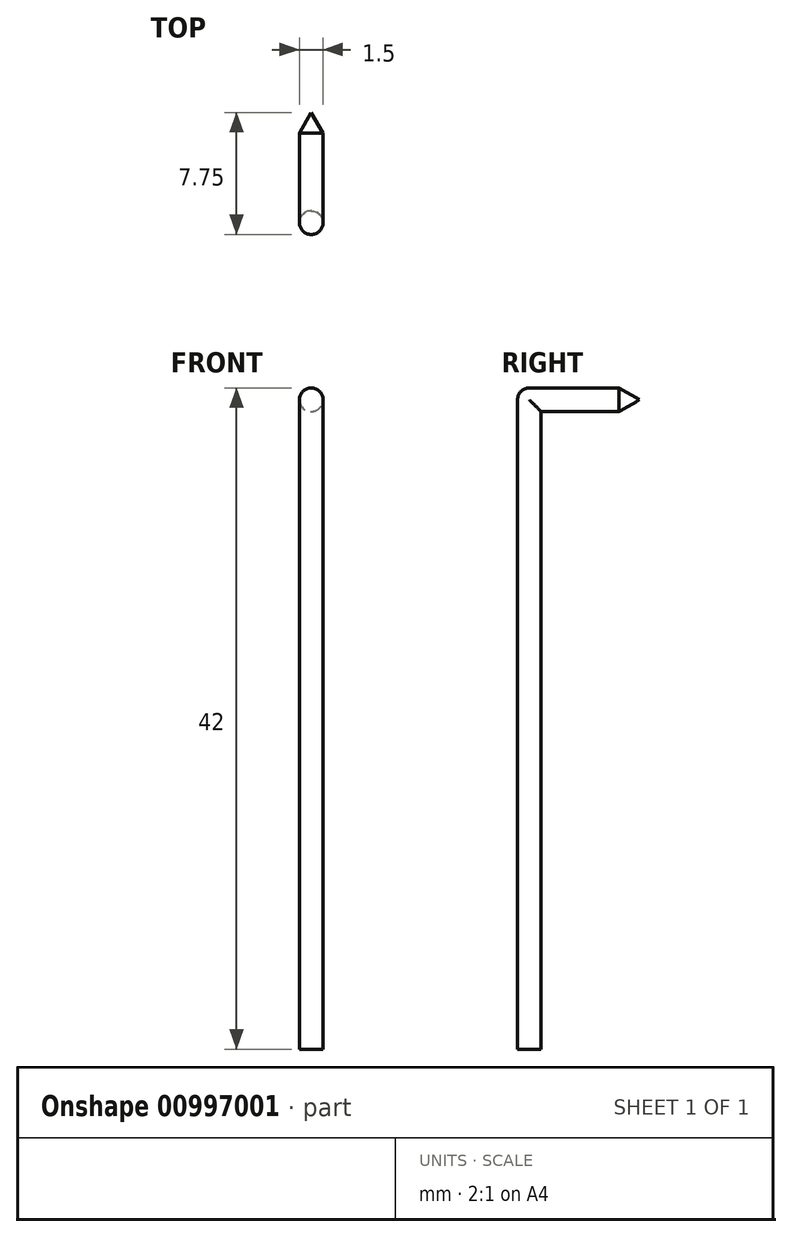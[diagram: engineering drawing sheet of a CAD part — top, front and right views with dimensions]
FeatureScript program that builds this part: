
annotation { "Feature Type Name" : "Feature", "Feature Type Description" : "" }
export const myFeature = defineFeature(function(context is Context, id is Id, definition is map)
    precondition{}
    {
        {
            var Q0;
            Q0=qCreatedBy(makeId("Top.planeOp"),FACE);
            var sketch = newSketch(context, id + "F0", { "sketchPlane" : qUnion([Q0])});
            skCircle(sketch, "E0", {"center": v(0, 0) * mm, "radius": 0.75 * mm});
            skLineSegment(sketch, "E1.bottom", {"start": v(-0.75, 0) * mm, "end": v(0.75, 0) * mm});
            skLineSegment(sketch, "E1.top", {"start": v(-0.75, 7) * mm, "end": v(0.75, 7) * mm});
            skLineSegment(sketch, "E1.left", {"start": v(-0.75, 0) * mm, "end": v(-0.75, 7) * mm});
            skLineSegment(sketch, "E1.right", {"start": v(0.75, 0) * mm, "end": v(0.75, 7) * mm});
            skSolve(sketch);
        }
        {
            var Q0;
            Q0=makeQuery(id+"F0.imprint","IMPRINT",FACE,{"disambiguationData":[TD([[makeQuery(id+"F0.imprint","IMPRINT",EDGE,{"derivedFrom":sQuery(id+"F0.wireOp",EDGE,"E0")}),1.0]])]});
            extrude(context, id + "F1", {"entities" : qUnion([Q0]), "depth" : 42 * mm, "offsetDistance" : 25 * mm});
        }
        {
            var Q0;
            Q0=makeQuery(id+"F0.imprint","IMPRINT",FACE,{"disambiguationData":[TD([[makeQuery(id+"F0.imprint","IMPRINT",EDGE,{"derivedFrom":sQuery(id+"F0.wireOp",EDGE,"E1.top")}),-1.0]])]});
            extrude(context, id + "F2", {"entities" : qUnion([Q0]), "operationType" : NewBodyOperationType.ADD, "depth" : 42 * mm, "offsetDistance" : 25 * mm, "hasSecondDirection" : true, "secondDirectionOppositeDirection" : false, "secondDirectionDepth" : 40.5 * mm});
        }
        {
            var Q0;
            {var subQ0=sQuery(id+"F0.wireOp",EDGE,"E1.top");Q0=makeQuery(id+"F0powoGMsJJjLha_1.opChamfer","BLEND_EDGE",EDGE,{"blendedFrom":[makeQuery(id+"F2.opExtrude","SWEPT_EDGE",EDGE,{"disambiguationData":[OSD([subQ0,sQuery(id+"F0.wireOp",EDGE,"E1.left")])]}),makeQuery(id+"F2.opExtrude","CAP_EDGE",EDGE,{"disambiguationData":[OSD([subQ0])],"isStart":false})],"blendedInto":[]});}
            var Q1;
            {var subQ0=sQuery(id+"F0.wireOp",EDGE,"E1.top");Q1=makeQuery(id+"F0powoGMsJJjLha_1.opChamfer","BLEND_EDGE",EDGE,{"blendedFrom":[makeQuery(id+"F2.opExtrude","SWEPT_EDGE",EDGE,{"disambiguationData":[OSD([subQ0,sQuery(id+"F0.wireOp",EDGE,"E1.right")])]}),makeQuery(id+"F2.opExtrude","CAP_EDGE",EDGE,{"disambiguationData":[OSD([subQ0])],"isStart":false})],"blendedInto":[]});}
            var Q2;
            {var subQ0=sQuery(id+"F0.wireOp",EDGE,"E1.top");Q2=makeQuery(id+"F0powoGMsJJjLha_1.opChamfer","BLEND_EDGE",EDGE,{"blendedFrom":[makeQuery(id+"F2.opExtrude","SWEPT_EDGE",EDGE,{"disambiguationData":[OSD([subQ0,sQuery(id+"F0.wireOp",EDGE,"E1.left")])]}),makeQuery(id+"F2.opExtrude","CAP_EDGE",EDGE,{"disambiguationData":[OSD([subQ0])],"isStart":true})],"blendedInto":[]});}
            var Q3;
            {var subQ0=sQuery(id+"F0.wireOp",EDGE,"E1.top");Q3=makeQuery(id+"F0powoGMsJJjLha_1.opChamfer","BLEND_EDGE",EDGE,{"blendedFrom":[makeQuery(id+"F2.opExtrude","SWEPT_EDGE",EDGE,{"disambiguationData":[OSD([subQ0,sQuery(id+"F0.wireOp",EDGE,"E1.right")])]}),makeQuery(id+"F2.opExtrude","CAP_EDGE",EDGE,{"disambiguationData":[OSD([subQ0])],"isStart":true})],"blendedInto":[]});}
            var Q4;
            Q4=makeQuery(id+"F1.opExtrude","CAP_EDGE",EDGE,{"disambiguationData":[OSD([sQuery(id+"F0.wireOp",EDGE,"E0")])],"isStart":false});
            var Q5;
            Q5=makeQuery(id+"F2.opExtrude","CAP_EDGE",EDGE,{"disambiguationData":[OSD([sQuery(id+"F0.wireOp",EDGE,"E1.left")])],"isStart":true});
            var Q6;
            Q6=makeQuery(id+"F2.opExtrude","CAP_EDGE",EDGE,{"disambiguationData":[OSD([sQuery(id+"F0.wireOp",EDGE,"E1.right")])],"isStart":true});
            fillet(context, id + "F3", {"entities" : qUnion([Q0, Q1, Q2, Q3, Q4, Q5, Q6]), "radius" : 0.75 * mm, "tangentPropagation" : true, "allowEdgeOverflow" : false});
        }
        {
            var Q0;
            Q0=makeQuery(id+"F3.opFillet","BLEND_EDGE",EDGE,{"blendedFrom":[makeQuery(id+"F2.opExtrude","CAP_EDGE",EDGE,{"disambiguationData":[OSD([sQuery(id+"F0.wireOp",EDGE,"E1.left")])],"isStart":true}),makeQuery(id+"F2.opExtrude","SWEPT_FACE",FACE,{"disambiguationData":[OSD([sQuery(id+"F0.wireOp",EDGE,"E1.top")])]})],"blendedInto":[makeQuery(id+"F2.opExtrude","SWEPT_FACE",FACE,{"disambiguationData":[OSD([sQuery(id+"F0.wireOp",EDGE,"E1.top")])]})]});
            chamfer(context, id + "F4", {"entities" : qUnion([Q0]), "chamferType" : ChamferType.OFFSET_ANGLE, "width" : 0.75 * mm, "oppositeDirection" : false, "angle" : 60 * degree, "tangentPropagation" : true});
        }
    });
